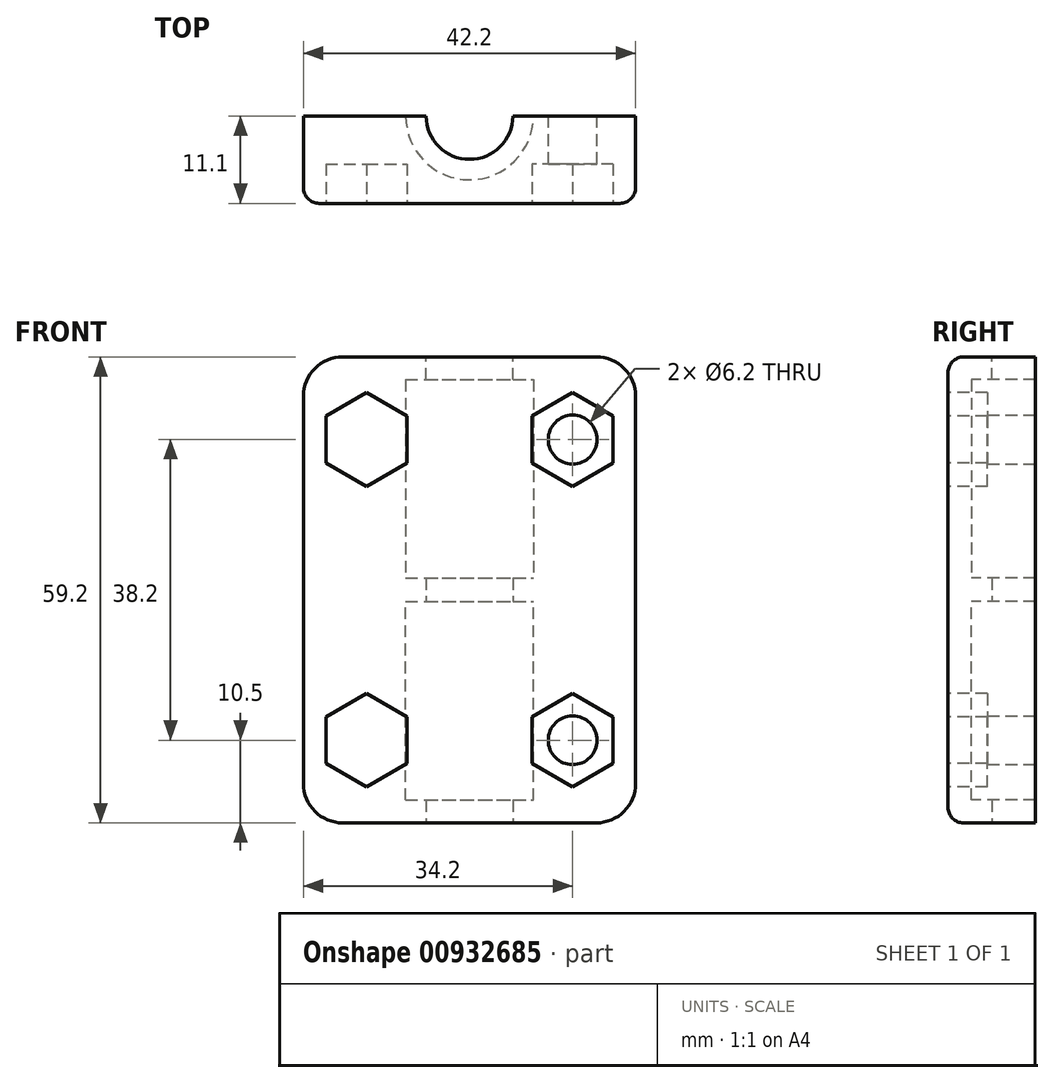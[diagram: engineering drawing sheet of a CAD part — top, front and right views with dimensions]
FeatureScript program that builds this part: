
annotation { "Feature Type Name" : "Feature", "Feature Type Description" : "" }
export const myFeature = defineFeature(function(context is Context, id is Id, definition is map)
    precondition{}
    {
        {
            var Q0;
            Q0=qCreatedBy(makeId("Top.planeOp"),FACE);
            var sketch = newSketch(context, id + "F0", { "sketchPlane" : qUnion([Q0])});
            skLineSegment(sketch, "E0.bottom", {"start": v(-21.1, 11.1) * mm, "end": v(21.1, 11.1) * mm});
            skLineSegment(sketch, "E0.top", {"start": v(-21.1, -11.1) * mm, "end": v(21.1, -11.1) * mm});
            skLineSegment(sketch, "E0.left", {"start": v(-21.1, 11.1) * mm, "end": v(-21.1, -11.1) * mm});
            skLineSegment(sketch, "E0.right", {"start": v(21.1, 11.1) * mm, "end": v(21.1, -11.1) * mm});
            skCircle(sketch, "E1", {"center": v(0, 0) * mm, "radius": 5.5 * mm});
            skCircle(sketch, "E2", {"center": v(0, 0) * mm, "radius": 8.1 * mm});
            skLineSegment(sketch, "E3", {"start": v(-21.1, 0) * mm, "end": v(21.1, 0) * mm});
            skPoint(sketch, "E3.endSnap0", {"position": v(21.1, 0) * mm});
            skSolve(sketch);
        }
        {
            var Q0;
            {var subQ5=sQuery(id+"F0.wireOp",EDGE,"E0.top");Q0=makeQuery(id+"F0.imprint","IMPRINT",FACE,{"disambiguationData":[TD([[makeQuery(id+"F0.imprint","IMPRINT",EDGE,{"derivedFrom":subQ5}),1.0]])]});}
            var Q1;
            {var subQ0=sQuery(id+"F0.wireOp",EDGE,"E3");var subQ1=sQuery(id+"F0.wireOp",EDGE,"E1");var subQ2=makeQuery(id+"F0.imprint","INTERSECT",VERTEX,{"disambiguationData":[OD(0.0)],"derivedFrom":[subQ1,subQ0]});Q1=makeQuery(id+"F0.imprint","IMPRINT",FACE,{"disambiguationData":[TD([[makeQuery(id+"F0.imprint","IMPRINT",EDGE,{"disambiguationData":[TD([[subQ2,-1.0]])],"derivedFrom":subQ1}),-1.0]])]});}
            extrude(context, id + "F1", {"entities" : qUnion([Q0, Q1]), "endBound" : BoundingType.SYMMETRIC, "depth" : 31 * mm, "offsetDistance" : 25 * mm});
        }
        {
            var Q0;
            {var subQ0=sQuery(id+"F0.wireOp",EDGE,"E3");var subQ1=sQuery(id+"F0.wireOp",EDGE,"E1");var subQ2=makeQuery(id+"F0.imprint","INTERSECT",VERTEX,{"disambiguationData":[OD(0.0)],"derivedFrom":[subQ1,subQ0]});Q0=makeQuery(id+"F0.imprint","IMPRINT",FACE,{"disambiguationData":[TD([[makeQuery(id+"F0.imprint","IMPRINT",EDGE,{"disambiguationData":[TD([[subQ2,-1.0]])],"derivedFrom":subQ1}),-1.0]])]});}
            extrude(context, id + "F2", {"entities" : qUnion([Q0]), "operationType" : NewBodyOperationType.REMOVE, "endBound" : BoundingType.SYMMETRIC, "oppositeDirection" : true, "depth" : 25.2 * mm, "offsetDistance" : 25 * mm});
        }
        {
            var Q0;
            Q0=qCreatedBy(makeId("Front.planeOp"),FACE);
            var sketch = newSketch(context, id + "F3", { "sketchPlane" : qUnion([Q0])});
            skCircle(sketch, "E4", {"center": v(13.1, -5) * mm, "radius": 3.1 * mm});
            skCircle(sketch, "E5.MirrorC", {"center": v(-13.1, -5) * mm, "radius": 3.1 * mm});
            skSolve(sketch);
        }
        {
            var Q0;
            Q0=makeQuery(id+"F3.imprint","IMPRINT",FACE,{"disambiguationData":[TD([[makeQuery(id+"F3.imprint","IMPRINT",EDGE,{"derivedFrom":sQuery(id+"F3.wireOp",EDGE,"E4")}),1.0]])]});
            var Q1;
            Q1=makeQuery(id+"F3.imprint","IMPRINT",FACE,{"disambiguationData":[TD([[makeQuery(id+"F3.imprint","IMPRINT",EDGE,{"derivedFrom":sQuery(id+"F3.wireOp",EDGE,"E5.MirrorC")}),-1.0]])]});
            var Q2;
            Q2=makeQuery(id+"F3.imprint","IMPRINT",FACE,{"disambiguationData":[TD([[makeQuery(id+"F3.imprint","IMPRINT",EDGE,{"derivedFrom":sQuery(id+"F3.wireOp",EDGE,"190f119f-4d8d-4553-abc9-2ea39d5197bc0.MirrorC")}),-1.0]])]});
            var Q3;
            Q3=makeQuery(id+"F3.imprint","IMPRINT",FACE,{"disambiguationData":[TD([[makeQuery(id+"F3.imprint","IMPRINT",EDGE,{"derivedFrom":sQuery(id+"F3.wireOp",EDGE,"77b27bc4-c542-429d-a95f-a5a226cd22150.MirrorC")}),1.0]])]});
            extrude(context, id + "F4", {"entities" : qUnion([Q0, Q1, Q2, Q3]), "operationType" : NewBodyOperationType.REMOVE, "endBound" : BoundingType.THROUGH_ALL, "depth" : 25 * mm, "offsetDistance" : 25 * mm});
        }
        {
            var Q0;
            Q0=makeQuery(id+"F1.opExtrude","CAP_FACE",FACE,{"disambiguationData":[OSD([sQuery(id+"F0.wireOp",EDGE,"E0.top"),sQuery(id+"F0.wireOp",EDGE,"E0.left"),sQuery(id+"F0.wireOp",EDGE,"E0.right"),sQuery(id+"F0.wireOp",EDGE,"E1"),sQuery(id+"F0.wireOp",EDGE,"E3")])],"isStart":false});
            cPlane(context, id + "F5", {"entities" : qUnion([Q0]), "cplaneType" : CPlaneType.OFFSET, "offset" : 1.4 * mm, "oppositeDirection" : true, "width" : 150 * mm, "height" : 150 * mm});
        }
        {
            var Q0;
            Q0=makeQuery(id+"F1.opExtrude","SWEPT_FACE",FACE,{"disambiguationData":[OSD([sQuery(id+"F0.wireOp",EDGE,"E0.top")])]});
            var sketch = newSketch(context, id + "F6", { "sketchPlane" : qUnion([Q0])});
            skCircle(sketch, "E6.cCircle", {"center": v(13.1, -5) * mm, "radius": 5.15 * mm, "construction": true});
            skLineSegment(sketch, "E6.0", {"start": v(7.95, -7.97) * mm, "end": v(7.95, -2.03) * mm});
            skLineSegment(sketch, "E6.1", {"start": v(7.95, -2.03) * mm, "end": v(13.1, 0.95) * mm});
            skLineSegment(sketch, "E6.2", {"start": v(13.1, 0.95) * mm, "end": v(18.25, -2.03) * mm});
            skLineSegment(sketch, "E6.3", {"start": v(18.25, -2.03) * mm, "end": v(18.25, -7.97) * mm});
            skLineSegment(sketch, "E6.4", {"start": v(18.25, -7.97) * mm, "end": v(13.1, -10.95) * mm});
            skLineSegment(sketch, "E6.5", {"start": v(13.1, -10.95) * mm, "end": v(7.95, -7.97) * mm});
            skPoint(sketch, "E6.0.midPoint", {"position": v(7.95, -5) * mm});
            skLineSegment(sketch, "E7.MirrorCS", {"start": v(-13.1, -10.95) * mm, "end": v(-7.95, -7.97) * mm});
            skLineSegment(sketch, "E8.MirrorCS", {"start": v(-7.95, -7.97) * mm, "end": v(-7.95, -2.03) * mm});
            skLineSegment(sketch, "E9.MirrorCS", {"start": v(-7.95, -2.03) * mm, "end": v(-13.1, 0.95) * mm});
            skLineSegment(sketch, "E10.MirrorCS", {"start": v(-13.1, 0.95) * mm, "end": v(-18.25, -2.03) * mm});
            skLineSegment(sketch, "E11.MirrorCS", {"start": v(-18.25, -2.03) * mm, "end": v(-18.25, -7.97) * mm});
            skLineSegment(sketch, "E12.MirrorCS", {"start": v(-18.25, -7.97) * mm, "end": v(-13.1, -10.95) * mm});
            skSolve(sketch);
        }
        {
            var Q0;
            Q0=makeQuery(id+"F6.imprint","IMPRINT",FACE,{"disambiguationData":[TD([[makeQuery(id+"F6.imprint","IMPRINT",EDGE,{"derivedFrom":sQuery(id+"F6.wireOp",EDGE,"E6.0")}),-1.0]])]});
            var Q1;
            Q1=makeQuery(id+"F6.imprint","IMPRINT",FACE,{"disambiguationData":[TD([[makeQuery(id+"F6.imprint","IMPRINT",EDGE,{"derivedFrom":sQuery(id+"F6.wireOp",EDGE,"E7.MirrorCS")}),1.0]])]});
            extrude(context, id + "F7", {"entities" : qUnion([Q0, Q1]), "operationType" : NewBodyOperationType.REMOVE, "oppositeDirection" : true, "depth" : 5 * mm, "offsetDistance" : 25 * mm});
        }
        {
            var Q0;
            Q0=makeQuery(id+"F1.opExtrude","SWEPT_BODY",BODY,{"disambiguationData":[OSD([sQuery(id+"F0.wireOp",EDGE,"E0.top"),sQuery(id+"F0.wireOp",EDGE,"E0.left"),sQuery(id+"F0.wireOp",EDGE,"E0.right"),sQuery(id+"F0.wireOp",EDGE,"E1"),sQuery(id+"F0.wireOp",EDGE,"E3")])]});
            var Q1;
            Q1=qCreatedBy(id+"F5.planeOp",FACE);
            mirror(context, id + "F8", {"operationType" : NewBodyOperationType.ADD, "entities" : qUnion([Q0]), "mirrorPlane" : qUnion([Q1])});
        }
        {
            var Q0;
            Q0=makeQuery(id+"F8.opPattern","COPY",EDGE,{"derivedFrom":makeQuery(id+"F1.opExtrude","CAP_EDGE",EDGE,{"disambiguationData":[OSD([sQuery(id+"F0.wireOp",EDGE,"E0.right")])],"isStart":true}),"instanceName":"1"});
            var Q1;
            Q1=makeQuery(id+"F1.opExtrude","CAP_EDGE",EDGE,{"disambiguationData":[OSD([sQuery(id+"F0.wireOp",EDGE,"E0.right")])],"isStart":true});
            var Q2;
            Q2=makeQuery(id+"F1.opExtrude","CAP_EDGE",EDGE,{"disambiguationData":[OSD([sQuery(id+"F0.wireOp",EDGE,"E0.left")])],"isStart":true});
            var Q3;
            Q3=makeQuery(id+"F8.opPattern","COPY",EDGE,{"derivedFrom":makeQuery(id+"F1.opExtrude","CAP_EDGE",EDGE,{"disambiguationData":[OSD([sQuery(id+"F0.wireOp",EDGE,"E0.left")])],"isStart":true}),"instanceName":"1"});
            fillet(context, id + "F9", {"entities" : qUnion([Q0, Q1, Q2, Q3]), "radius" : 5 * mm, "tangentPropagation" : true, "allowEdgeOverflow" : false});
        }
        {
            var Q0;
            {var subQ0=makeQuery(id+"F1.opExtrude","SWEPT_EDGE",EDGE,{"disambiguationData":[OSD([sQuery(id+"F0.wireOp",EDGE,"E0.top"),sQuery(id+"F0.wireOp",EDGE,"E0.right")])]});Q0=makeQuery(id+"F8.boolean.opBoolean","MERGE",EDGE,{"derivedFrom":[subQ0,makeQuery(id+"F8.opPattern","COPY",EDGE,{"derivedFrom":subQ0,"instanceName":"1"})]});}
            var Q1;
            {var subQ0=makeQuery(id+"F1.opExtrude","SWEPT_FACE",FACE,{"disambiguationData":[OSD([sQuery(id+"F0.wireOp",EDGE,"E0.top")])]});Q1=makeQuery(id+"F9.opFillet","BLEND_EDGE",EDGE,{"blendedFrom":[makeQuery(id+"F1.opExtrude","CAP_EDGE",EDGE,{"disambiguationData":[OSD([sQuery(id+"F0.wireOp",EDGE,"E0.right")])],"isStart":true}),makeQuery(id+"F8.boolean.opBoolean","MERGE",FACE,{"derivedFrom":[subQ0,makeQuery(id+"F8.opPattern","COPY",FACE,{"derivedFrom":subQ0,"instanceName":"1"})]})],"blendedInto":[makeQuery(id+"F8.boolean.opBoolean","MERGE",FACE,{"derivedFrom":[subQ0,makeQuery(id+"F8.opPattern","COPY",FACE,{"derivedFrom":subQ0,"instanceName":"1"})]})]});}
            fillet(context, id + "F10", {"entities" : qUnion([Q0, Q1]), "radius" : 2 * mm, "tangentPropagation" : true, "allowEdgeOverflow" : false});
        }
    });
